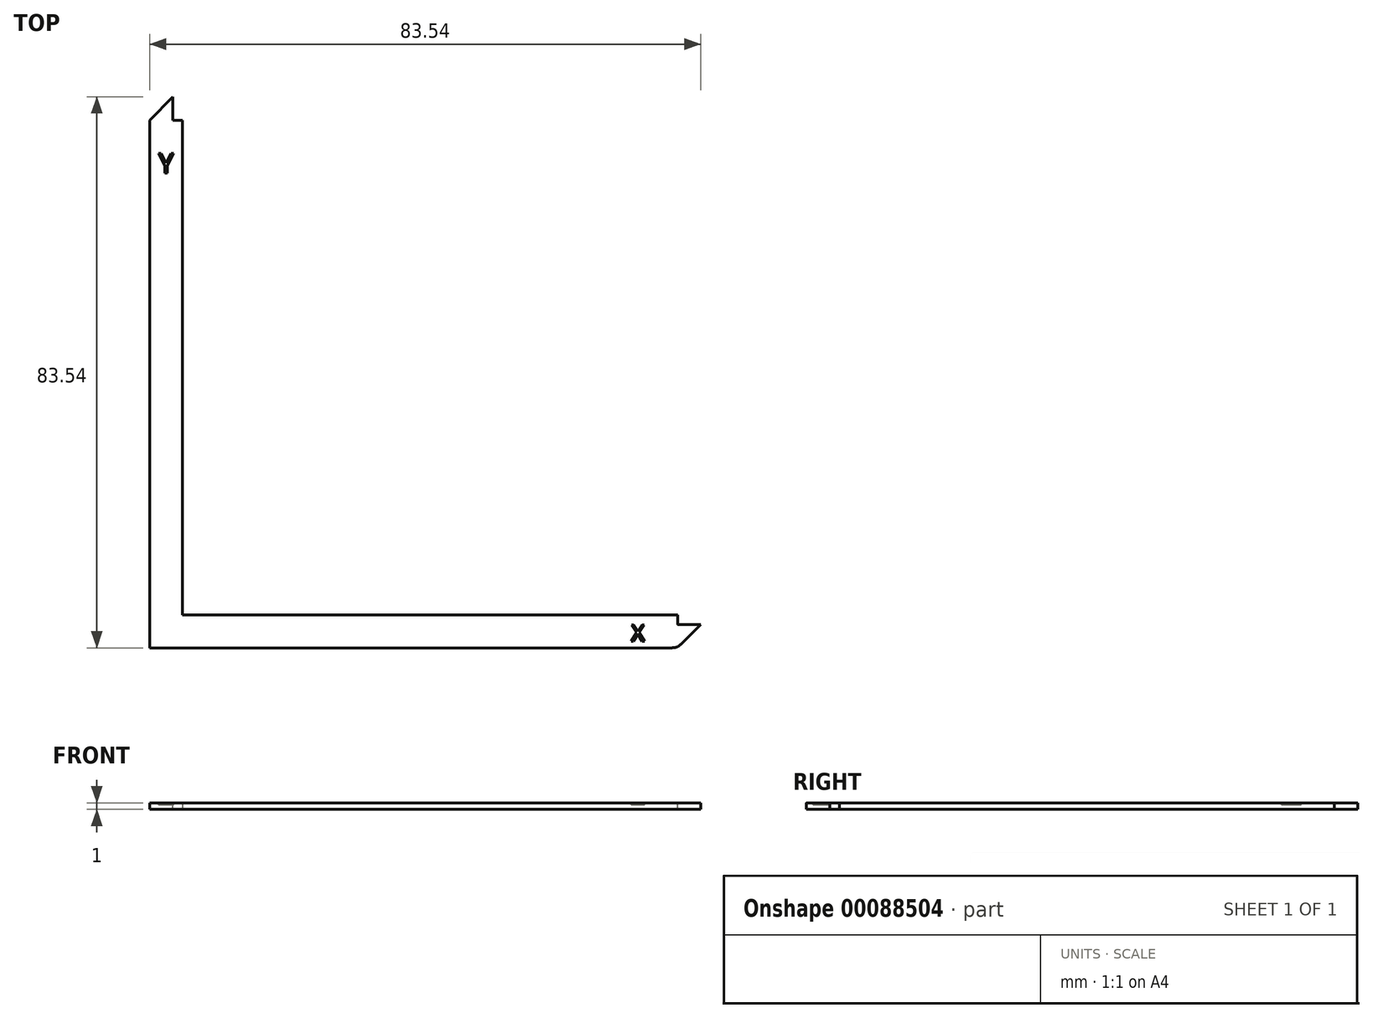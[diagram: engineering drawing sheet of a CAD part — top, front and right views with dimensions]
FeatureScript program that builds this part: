
annotation { "Feature Type Name" : "Feature", "Feature Type Description" : "" }
export const myFeature = defineFeature(function(context is Context, id is Id, definition is map)
    precondition{}
    {
        {
            var Q0;
            Q0=qCreatedBy(makeId("Top.planeOp"),FACE);
            var sketch = newSketch(context, id + "F0", { "sketchPlane" : qUnion([Q0])});
            skLineSegment(sketch, "E0.bottom", {"start": v(0, 0) * mm, "end": v(5, 0) * mm});
            skLineSegment(sketch, "E0.top", {"start": v(0, 80) * mm, "end": v(5, 80) * mm});
            skLineSegment(sketch, "E0.left", {"start": v(0, 0) * mm, "end": v(0, 80) * mm});
            skLineSegment(sketch, "E0.right", {"start": v(5, 5) * mm, "end": v(5, 80) * mm});
            skLineSegment(sketch, "E1.bottom", {"start": v(0, 0) * mm, "end": v(80, 0) * mm});
            skLineSegment(sketch, "E1.top", {"start": v(5, 5) * mm, "end": v(80, 5) * mm});
            skLineSegment(sketch, "E1.left", {"start": v(0, 0) * mm, "end": v(0, 5) * mm});
            skLineSegment(sketch, "E1.right", {"start": v(80, 0) * mm, "end": v(80, 5) * mm});
            skSolve(sketch);
        }
        {
            var Q0;
            Q0=makeQuery(id+"F0.imprint","IMPRINT",FACE,{"disambiguationData":[TD([[makeQuery(id+"F0.imprint","IMPRINT",EDGE,{"derivedFrom":sQuery(id+"F0.wireOp",EDGE,"E0.top")}),-1.0]])]});
            extrude(context, id + "F1", {"entities" : qUnion([Q0]), "depth" : 1 * mm});
        }
        {
            var Q0;
            Q0=makeQuery(id+"F1.opExtrude","CAP_FACE",FACE,{"disambiguationData":[OSD([sQuery(id+"F0.wireOp",EDGE,"E0.top"),sQuery(id+"F0.wireOp",EDGE,"E0.left"),sQuery(id+"F0.wireOp",EDGE,"E0.right"),sQuery(id+"F0.wireOp",EDGE,"E1.bottom"),sQuery(id+"F0.wireOp",EDGE,"E1.top"),sQuery(id+"F0.wireOp",EDGE,"E1.left"),sQuery(id+"F0.wireOp",EDGE,"E1.right")])],"isStart":false});
            var sketch = newSketch(context, id + "F2", { "sketchPlane" : qUnion([Q0])});
            skPoint(sketch, "E2", {"position": v(0, 80) * mm});
            skPoint(sketch, "E3", {"position": v(80, 0) * mm});
            skLineSegment(sketch, "E4", {"start": v(0, 80) * mm, "end": v(3.54, 83.54) * mm});
            skLineSegment(sketch, "E5", {"start": v(3.54, 83.54) * mm, "end": v(3.54, 80) * mm});
            skLineSegment(sketch, "E6", {"start": v(3.54, 80) * mm, "end": v(0, 80) * mm});
            skLineSegment(sketch, "E7", {"start": v(80, 0) * mm, "end": v(83.54, 3.54) * mm});
            skLineSegment(sketch, "E8", {"start": v(83.54, 3.54) * mm, "end": v(80, 3.54) * mm});
            skLineSegment(sketch, "E9", {"start": v(80, 3.54) * mm, "end": v(80, 0) * mm});
            skSolve(sketch);
        }
        {
            var Q0;
            Q0=makeQuery(id+"F2.imprint","IMPRINT",FACE,{"disambiguationData":[TD([[makeQuery(id+"F2.imprint","IMPRINT",EDGE,{"derivedFrom":sQuery(id+"F2.wireOp",EDGE,"E4")}),-1.0]])]});
            var Q1;
            Q1=makeQuery(id+"F2.imprint","IMPRINT",FACE,{"disambiguationData":[TD([[makeQuery(id+"F2.imprint","IMPRINT",EDGE,{"derivedFrom":sQuery(id+"F2.wireOp",EDGE,"E7")}),1.0]])]});
            var Q2;
            Q2=makeQuery(id+"F1.opExtrude","CAP_FACE",FACE,{"disambiguationData":[OSD([sQuery(id+"F0.wireOp",EDGE,"E0.top"),sQuery(id+"F0.wireOp",EDGE,"E0.left"),sQuery(id+"F0.wireOp",EDGE,"E0.right"),sQuery(id+"F0.wireOp",EDGE,"E1.bottom"),sQuery(id+"F0.wireOp",EDGE,"E1.top"),sQuery(id+"F0.wireOp",EDGE,"E1.left"),sQuery(id+"F0.wireOp",EDGE,"E1.right")])],"isStart":true});
            extrude(context, id + "F3", {"entities" : qUnion([Q0, Q1]), "operationType" : NewBodyOperationType.ADD, "endBound" : BoundingType.UP_TO_SURFACE, "oppositeDirection" : true, "endBoundEntityFace" : qUnion([Q2]), "depth" : 25 * mm});
        }
        {
            var Q0;
            Q0=makeQuery(id+"F3.boolean.opBoolean","MERGE",FACE,{"derivedFrom":[makeQuery(id+"F1.opExtrude","CAP_FACE",FACE,{"disambiguationData":[OSD([sQuery(id+"F0.wireOp",EDGE,"E0.top"),sQuery(id+"F0.wireOp",EDGE,"E0.left"),sQuery(id+"F0.wireOp",EDGE,"E0.right"),sQuery(id+"F0.wireOp",EDGE,"E1.bottom"),sQuery(id+"F0.wireOp",EDGE,"E1.top"),sQuery(id+"F0.wireOp",EDGE,"E1.left"),sQuery(id+"F0.wireOp",EDGE,"E1.right")])],"isStart":false}),makeQuery(id+"F3.opExtrude","CAP_FACE",FACE,{"disambiguationData":[OSD([sQuery(id+"F2.wireOp",EDGE,"E4"),sQuery(id+"F2.wireOp",EDGE,"E5"),sQuery(id+"F2.wireOp",EDGE,"E6")])],"isStart":true}),makeQuery(id+"F3.opExtrude","CAP_FACE",FACE,{"disambiguationData":[OSD([sQuery(id+"F2.wireOp",EDGE,"E7"),sQuery(id+"F2.wireOp",EDGE,"E8"),sQuery(id+"F2.wireOp",EDGE,"E9")])],"isStart":true})]});
            var sketch = newSketch(context, id + "F4", { "sketchPlane" : qUnion([Q0])});
            skText(sketch, "E10", { "text": "Y", "fontName": "OpenSans-Regular.ttf"});
            skText(sketch, "E11", { "text": "X", "fontName": "OpenSans-Regular.ttf"});
            const initialGuessF4  = {"E10": [0.00133, 0.072, 1, 0, 0.003], "E11": [0.073, 0.001, 1, 0, 0.0025]};
            skSetInitialGuess(sketch, initialGuessF4);
            skSolve(sketch);
        }
        {
            var Q0;
            Q0 = qSketchRegion(id + "F4", true);
            extrude(context, id + "F5", {"entities" : qUnion([Q0]), "operationType" : NewBodyOperationType.REMOVE, "oppositeDirection" : true, "depth" : 0.3 * mm});
        }
        {
            var Q0;
            Q0=makeQuery(id+"F1.opExtrude","CAP_EDGE",EDGE,{"disambiguationData":[OSD([sQuery(id+"F0.wireOp",EDGE,"E1.right")])],"isStart":true});
            fillet(context, id + "F6", {"entities" : qUnion([Q0]), "radius" : .1 * mm, "tangentPropagation" : true, "allowEdgeOverflow" : false});
        }
        {
            var Q0;
            Q0=makeQuery(id+"F1.opExtrude","SWEPT_EDGE",EDGE,{"disambiguationData":[OSD([sQuery(id+"F0.wireOp",EDGE,"E1.bottom"),sQuery(id+"F0.wireOp",EDGE,"E1.left")])]});
            fillet(context, id + "F7", {"entities" : qUnion([Q0]), "radius" : 2 * mm, "tangentPropagation" : true, "allowEdgeOverflow" : false});
        }
    });
